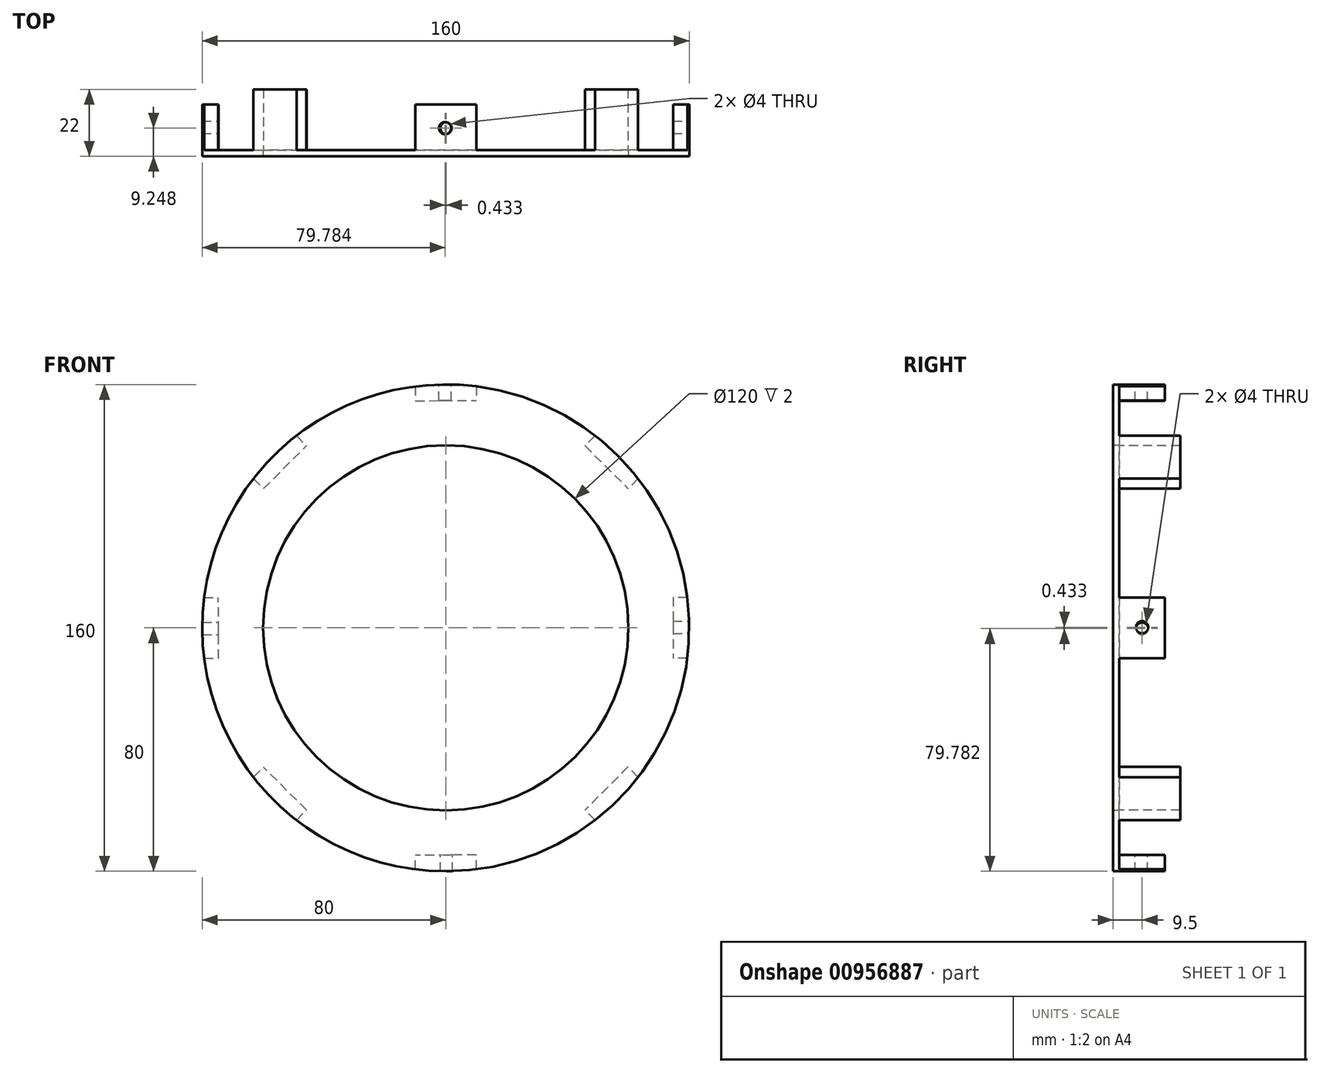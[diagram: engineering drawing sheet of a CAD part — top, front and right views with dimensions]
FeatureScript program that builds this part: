
annotation { "Feature Type Name" : "Feature", "Feature Type Description" : "" }
export const myFeature = defineFeature(function(context is Context, id is Id, definition is map)
    precondition{}
    {
        {
            var Q0;
            Q0=qCreatedBy(makeId("Front.planeOp"),FACE);
            var sketch = newSketch(context, id + "F0", { "sketchPlane" : qUnion([Q0])});
            skCircle(sketch, "E0", {"center": v(0, 0) * mm, "radius": 80 * mm});
            skSolve(sketch);
        }
        {
            var Q0;
            Q0 = qSketchRegion(id + "F0", true);
            extrude(context, id + "F1", {"entities" : qUnion([Q0]), "depth" : 2 * mm, "offsetDistance" : 25 * mm});
        }
        {
            var Q0;
            Q0=makeQuery(id+"F1.opExtrude","CAP_FACE",FACE,{"disambiguationData":[OSD([sQuery(id+"F0.wireOp",EDGE,"E0")])],"isStart":false});
            var sketch = newSketch(context, id + "F2", { "sketchPlane" : qUnion([Q0])});
            skCircle(sketch, "E1", {"center": v(0, 0) * mm, "radius": 60 * mm});
            skSolve(sketch);
        }
        {
            var Q0;
            Q0 = qSketchRegion(id + "F2", true);
            extrude(context, id + "F3", {"entities" : qUnion([Q0]), "operationType" : NewBodyOperationType.REMOVE, "oppositeDirection" : true, "depth" : 25 * mm, "offsetDistance" : 25 * mm});
        }
        {
            var Q0;
            Q0=makeQuery(id+"F0.imprint","IMPRINT",FACE,{"disambiguationData":[TD([[makeQuery(id+"F0.imprint","IMPRINT",EDGE,{"derivedFrom":sQuery(id+"F0.wireOp",EDGE,"E0")}),1.0]])]});
            var sketch = newSketch(context, id + "F4", { "sketchPlane" : qUnion([Q0])});
            skPoint(sketch, "E2", {"position": v(-80, 0) * mm});
            skPoint(sketch, "E3", {"position": v(-79.37, -10) * mm});
            skPoint(sketch, "E4", {"position": v(-79.37, 10) * mm});
            skLineSegment(sketch, "E5", {"start": v(-79.37, 10) * mm, "end": v(-74.71, 10) * mm});
            skLineSegment(sketch, "E6", {"start": v(-79.37, -10) * mm, "end": v(-74.66, -10) * mm});
            skLineSegment(sketch, "E7", {"start": v(-74.66, -10) * mm, "end": v(-74.71, 10) * mm});
            skArc(sketch, "E8", {"start": v(-79.37, 10) * mm, "mid": v(-80, 0) * mm, "end": v(-79.37, -10) * mm});
            skPoint(sketch, "E9.1.0", {"position": v(10, -79.37) * mm});
            skArc(sketch, "E9.1.1", {"start": v(-10, -79.37) * mm, "mid": v(0, -80) * mm, "end": v(10, -79.37) * mm});
            skPoint(sketch, "E9.1.2", {"position": v(-10, -79.37) * mm});
            skLineSegment(sketch, "E9.1.3", {"start": v(10, -74.66) * mm, "end": v(-10, -74.71) * mm});
            skLineSegment(sketch, "E9.1.4", {"start": v(10, -79.37) * mm, "end": v(10, -74.66) * mm});
            skLineSegment(sketch, "E9.1.5", {"start": v(-10, -79.37) * mm, "end": v(-10, -74.71) * mm});
            skPoint(sketch, "E9.1.6", {"position": v(0, -80) * mm});
            skPoint(sketch, "E9.2.0", {"position": v(79.37, 10) * mm});
            skArc(sketch, "E9.2.1", {"start": v(79.37, -10) * mm, "mid": v(80, 0) * mm, "end": v(79.37, 10) * mm});
            skPoint(sketch, "E9.2.2", {"position": v(79.37, -10) * mm});
            skLineSegment(sketch, "E9.2.3", {"start": v(74.66, 10) * mm, "end": v(74.71, -10) * mm});
            skLineSegment(sketch, "E9.2.4", {"start": v(79.37, 10) * mm, "end": v(74.66, 10) * mm});
            skLineSegment(sketch, "E9.2.5", {"start": v(79.37, -10) * mm, "end": v(74.71, -10) * mm});
            skPoint(sketch, "E9.2.6", {"position": v(80, 0) * mm});
            skPoint(sketch, "E9.3.0", {"position": v(-10, 79.37) * mm});
            skArc(sketch, "E9.3.1", {"start": v(10, 79.37) * mm, "mid": v(0, 80) * mm, "end": v(-10, 79.37) * mm});
            skPoint(sketch, "E9.3.2", {"position": v(10, 79.37) * mm});
            skLineSegment(sketch, "E9.3.3", {"start": v(-10, 74.66) * mm, "end": v(10, 74.71) * mm});
            skLineSegment(sketch, "E9.3.4", {"start": v(-10, 79.37) * mm, "end": v(-10, 74.66) * mm});
            skLineSegment(sketch, "E9.3.5", {"start": v(10, 79.37) * mm, "end": v(10, 74.71) * mm});
            skPoint(sketch, "E9.3.6", {"position": v(0, 80) * mm});
            skSolve(sketch);
        }
        {
            var Q0;
            Q0 = qSketchRegion(id + "F4", true);
            extrude(context, id + "F5", {"entities" : qUnion([Q0]), "operationType" : NewBodyOperationType.ADD, "oppositeDirection" : true, "depth" : 15 * mm, "offsetDistance" : 25 * mm});
        }
        {
            var Q0;
            Q0=makeQuery(id+"F5.opExtrude","SWEPT_FACE",FACE,{"disambiguationData":[OSD([sQuery(id+"F4.wireOp",EDGE,"E9.3.3")])]});
            var sketch = newSketch(context, id + "F6", { "sketchPlane" : qUnion([Q0])});
            skCircle(sketch, "E10", {"center": v(0, -7.25) * mm, "radius": 2 * mm});
            skSolve(sketch);
        }
        {
            var Q0;
            Q0=makeQuery(id+"F6.imprint","IMPRINT",FACE,{"disambiguationData":[TD([[makeQuery(id+"F6.imprint","IMPRINT",EDGE,{"derivedFrom":sQuery(id+"F6.wireOp",EDGE,"E10")}),1.0]])]});
            var Q1;
            Q1=sQuery(id+"F6.wireOp",EDGE,"E10");
            extrude(context, id + "F7", {"entities" : qUnion([Q0]), "operationType" : NewBodyOperationType.REMOVE, "surfaceEntities" : qUnion([Q1]), "endBound" : BoundingType.THROUGH_ALL, "depth" : 25 * mm, "offsetDistance" : 25 * mm, "hasSecondDirection" : true, "secondDirectionBound" : SecondDirectionBoundingType.THROUGH_ALL, "secondDirectionOppositeDirection" : true, "secondDirectionDepth" : 25 * mm});
        }
        {
            var Q0;
            Q0=makeQuery(id+"F5.opExtrude","SWEPT_FACE",FACE,{"disambiguationData":[OSD([sQuery(id+"F4.wireOp",EDGE,"E7")])]});
            var sketch = newSketch(context, id + "F8", { "sketchPlane" : qUnion([Q0])});
            skCircle(sketch, "E11", {"center": v(7.5, 0) * mm, "radius": 2 * mm});
            skPoint(sketch, "E11.centerSnap0", {"position": v(7.5, -9.8) * mm});
            skSolve(sketch);
        }
        {
            var Q0;
            Q0 = qSketchRegion(id + "F8", true);
            extrude(context, id + "F9", {"entities" : qUnion([Q0]), "operationType" : NewBodyOperationType.REMOVE, "endBound" : BoundingType.THROUGH_ALL, "oppositeDirection" : true, "depth" : 25 * mm, "offsetDistance" : 25 * mm, "hasSecondDirection" : true, "secondDirectionBound" : SecondDirectionBoundingType.THROUGH_ALL, "secondDirectionOppositeDirection" : false, "secondDirectionDepth" : 25 * mm});
        }
        {
            var Q0;
            Q0=makeQuery(id+"F0.imprint","IMPRINT",FACE,{"disambiguationData":[TD([[makeQuery(id+"F0.imprint","IMPRINT",EDGE,{"derivedFrom":sQuery(id+"F0.wireOp",EDGE,"E0")}),1.0]])]});
            var sketch = newSketch(context, id + "F10", { "sketchPlane" : qUnion([Q0])});
            skPoint(sketch, "E12", {"position": v(-49.05, -63.2) * mm});
            skPoint(sketch, "E13", {"position": v(-63.2, -49.05) * mm});
            skLineSegment(sketch, "E14", {"start": v(-63.2, -49.05) * mm, "end": v(-59.9, -45.76) * mm});
            skLineSegment(sketch, "E15", {"start": v(-49.05, -63.2) * mm, "end": v(-45.72, -59.86) * mm});
            skLineSegment(sketch, "E16", {"start": v(-45.72, -59.86) * mm, "end": v(-59.9, -45.76) * mm});
            skArc(sketch, "E17", {"start": v(-63.2, -49.05) * mm, "mid": v(-56.57, -56.57) * mm, "end": v(-49.05, -63.2) * mm});
            skPoint(sketch, "E18.1.0", {"position": v(63.2, -49.05) * mm});
            skArc(sketch, "E18.1.1", {"start": v(49.05, -63.2) * mm, "mid": v(56.57, -56.57) * mm, "end": v(63.2, -49.05) * mm});
            skPoint(sketch, "E18.1.2", {"position": v(49.05, -63.2) * mm});
            skLineSegment(sketch, "E18.1.3", {"start": v(59.86, -45.72) * mm, "end": v(45.76, -59.9) * mm});
            skLineSegment(sketch, "E18.1.4", {"start": v(63.2, -49.05) * mm, "end": v(59.86, -45.72) * mm});
            skLineSegment(sketch, "E18.1.5", {"start": v(49.05, -63.2) * mm, "end": v(45.76, -59.9) * mm});
            skPoint(sketch, "E18.2.0", {"position": v(49.05, 63.2) * mm});
            skArc(sketch, "E18.2.1", {"start": v(63.2, 49.05) * mm, "mid": v(56.57, 56.57) * mm, "end": v(49.05, 63.2) * mm});
            skPoint(sketch, "E18.2.2", {"position": v(63.2, 49.05) * mm});
            skLineSegment(sketch, "E18.2.3", {"start": v(45.72, 59.86) * mm, "end": v(59.9, 45.76) * mm});
            skLineSegment(sketch, "E18.2.4", {"start": v(49.05, 63.2) * mm, "end": v(45.72, 59.86) * mm});
            skLineSegment(sketch, "E18.2.5", {"start": v(63.2, 49.05) * mm, "end": v(59.9, 45.76) * mm});
            skPoint(sketch, "E18.3.0", {"position": v(-63.2, 49.05) * mm});
            skArc(sketch, "E18.3.1", {"start": v(-49.05, 63.2) * mm, "mid": v(-56.57, 56.57) * mm, "end": v(-63.2, 49.05) * mm});
            skPoint(sketch, "E18.3.2", {"position": v(-49.05, 63.2) * mm});
            skLineSegment(sketch, "E18.3.3", {"start": v(-59.86, 45.72) * mm, "end": v(-45.76, 59.9) * mm});
            skLineSegment(sketch, "E18.3.4", {"start": v(-63.2, 49.05) * mm, "end": v(-59.86, 45.72) * mm});
            skLineSegment(sketch, "E18.3.5", {"start": v(-49.05, 63.2) * mm, "end": v(-45.76, 59.9) * mm});
            skLineSegment(sketch, "E19.0", {"start": v(-49.05, -63.2) * mm, "end": v(-49.05, -63.2) * mm});
            skLineSegment(sketch, "E19.1", {"start": v(-49.05, -63.2) * mm, "end": v(-63.2, -49.05) * mm, "construction": true});
            skSolve(sketch);
        }
        {
            var Q0;
            Q0 = qSketchRegion(id + "F10", true);
            extrude(context, id + "F11", {"entities" : qUnion([Q0]), "operationType" : NewBodyOperationType.ADD, "oppositeDirection" : true, "depth" : 20 * mm, "offsetDistance" : 25 * mm});
        }
    });
